# Revit family: 8005 Napier 650
name_source: partatom
category: Lighting Fixtures
revit_build: Autodesk Revit 2018 (Build: 20170223_1515(x64)
units: mm (PartAtom-declared; Revit-internal decimal feet)

## family parameters
Always vertical = Yes
Cut with Voids When Loaded = No
Light Source = Yes
OmniClass Number = 23.80.70.00
OmniClass Title = Lighting
Part Type = Normal
Room Calculation Point = No
Round Connector Dimension = Use Diameter
Shared = No
Work Plane-Based = No

## types (1)
- CE
    Apparent Load = 20 VA
    Color Filter = 16777215
    Dimmable = No
    Dimming Lamp Color Temperature Shift = <None>
    Driver Included = Yes (Integral)
    Driver Required = Yes
    Efficacy (lm/W) = 46.32
    Electrical Class = 1
    Lamp = LED
    Light Source Fixed = Yes
    Location Rating = IP54
    Main Finish = Textured Black
    Main Material = Metal - Aluminium
    Photometric Web File = GNC-21459 Napier 650 Bollard.ies
    Power (W) = 8.7
    Prdouct Code = 8005
    Product Location = Outdoor
    Product Name = Napier LED 650 Bollard
    Product SKU = 1357006
    Tilt Angle = 0.00°

## geometry (parser evidence)
native form markers: Sweep x1
no freeform markers — native parametric forms only
